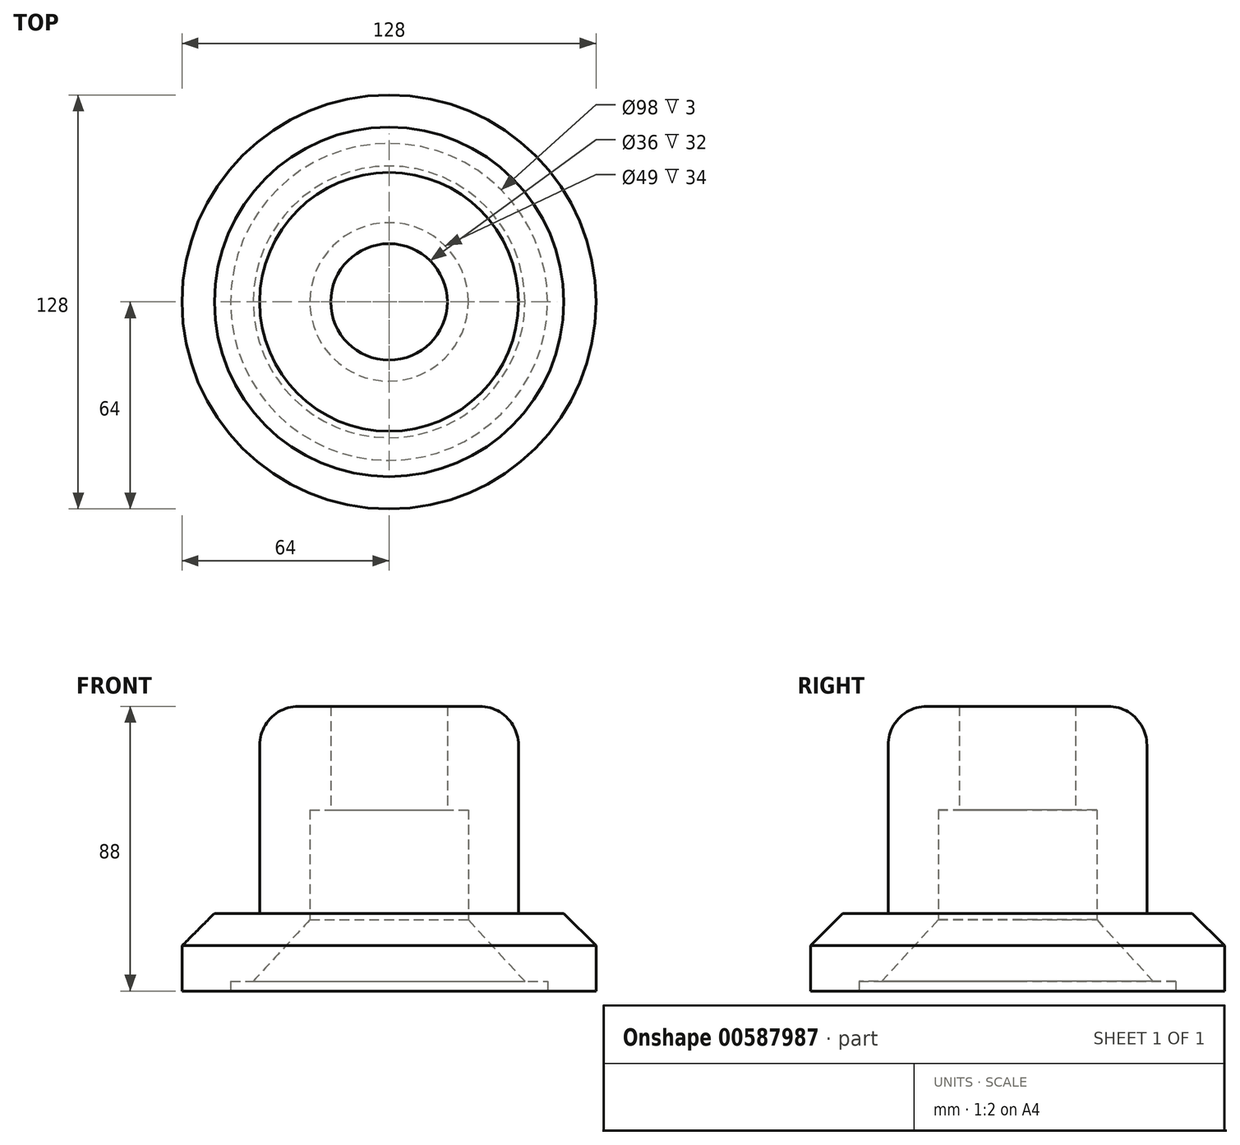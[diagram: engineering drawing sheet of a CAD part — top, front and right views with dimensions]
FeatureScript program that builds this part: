
annotation { "Feature Type Name" : "Feature", "Feature Type Description" : "" }
export const myFeature = defineFeature(function(context is Context, id is Id, definition is map)
    precondition{}
    {
        {
            var Q0;
            Q0=qCreatedBy(makeId("Right.planeOp"),FACE);
            var sketch = newSketch(context, id + "F0", { "sketchPlane" : qUnion([Q0])});
            skLineSegment(sketch, "E0", {"start": v(49, 0) * mm, "end": v(64, 0) * mm});
            skLineSegment(sketch, "E1", {"start": v(64, 14) * mm, "end": v(64, 0) * mm});
            skLineSegment(sketch, "E2", {"start": v(64, 14) * mm, "end": v(54, 24) * mm});
            skLineSegment(sketch, "E3", {"start": v(54, 24) * mm, "end": v(40, 24) * mm});
            skLineSegment(sketch, "E4", {"start": v(49, 0) * mm, "end": v(49, 3) * mm});
            skLineSegment(sketch, "E5", {"start": v(49, 3) * mm, "end": v(42, 3) * mm});
            skLineSegment(sketch, "E6", {"start": v(42, 3) * mm, "end": v(24.5, 22) * mm});
            skLineSegment(sketch, "E7", {"start": v(24.5, 22) * mm, "end": v(24.5, 56) * mm});
            skLineSegment(sketch, "E8", {"start": v(24.5, 56) * mm, "end": v(18, 56) * mm});
            skLineSegment(sketch, "E9", {"start": v(18, 56) * mm, "end": v(18, 88) * mm});
            skLineSegment(sketch, "E10", {"start": v(0, 0) * mm, "end": v(0, 39.34) * mm, "construction": true});
            skLineSegment(sketch, "E11", {"start": v(18, 88) * mm, "end": v(28, 88) * mm});
            skPoint(sketch, "E12", {"position": v(40, 88) * mm});
            skLineSegment(sketch, "E13", {"start": v(40, 24) * mm, "end": v(40, 76) * mm});
            skPoint(sketch, "E14", {"position": v(40, 76) * mm});
            skArc(sketch, "E15", {"start": v(40, 76) * mm, "mid": v(36.49, 84.49) * mm, "end": v(28, 88) * mm});
            skSolve(sketch);
        }
        {
            var Q0;
            Q0=makeQuery(id+"F0.imprint","IMPRINT",FACE,{"disambiguationData":[TD([[makeQuery(id+"F0.imprint","IMPRINT",EDGE,{"derivedFrom":sQuery(id+"F0.wireOp",EDGE,"E0")}),1.0]])]});
            var Q1;
            Q1=sQuery(id+"F0.wireOp",EDGE,"E10");
            revolve(context, id + "F1", {"entities" : qUnion([Q0]), "axis" : qUnion([Q1]), "revolveType" : RevolveType.FULL});
        }
    });
